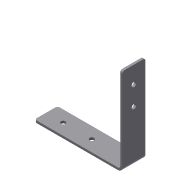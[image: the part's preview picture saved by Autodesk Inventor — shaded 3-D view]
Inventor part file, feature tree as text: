
AUTODESK INVENTOR PART (.ipt)
format: ipt  version: 2016 (Build 200138000, 138)  size: 123,392 bytes
history: native  units: in
note: dims shown in document units (in); Inventor stores cm internally (conversion verified against a paired STEP export)
features: sketch x5, hole x3, extrude x1, fillet x1, sheet_metal_op x1
ambient origin geometry x8: Origin, YZ Plane, XZ Plane, XY Plane, X Axis, Y Axis, Z Axis, Center Point
bodies: Body1 (feature_tree)
feature tree (11):
  extrude  "Extrusion3"  Depth=0.7874in
  fillet  "Fillet2"  Radius=0.0787in
  hole  "Hole3"  [1 undecoded]
  sheet_metal_op  "Fold1"
  hole  "Hole4"  [1 undecoded]
  hole  "Hole5"  [1 undecoded]
  sketch  "Sketch6"  dims[d42=5.9055in d43=0.7874in d44=0.0787in d45=0.0in]
  sketch  "Sketch7"  dims[d47=0.0787in d48=2.3622in]
  sketch  "Sketch8"  dims[d49=0.1575in d50=0.2362in d51=0.1575in d52=0.0787in d53=90.0deg d54=0.315in d55=0.8108in d56=0.0787in]
  sketch  "Sketch9"  dims[d57=0.0394in d58=0.1575in]
  sketch  "Sketch10"  dims[d59=0.0787in d60=90.0deg d61=0.0787in d62=0.1575in d63=0.2362in d64=0.1575in d65=0.0787in d66=90.0deg d67=0.315in d68=0.8108in d69=0.9843in d70=0.659in d71=0.1575in d72=0.2362in d73=0.1575in d74=0.0787in d75=90.0deg d76=0.315in d77=0.8108in]
note: 3 required parameter values undecoded (feature->parameter linkage not recoverable at this tier; creation-order binding heuristic only, values carry confidence <= 0.55)
